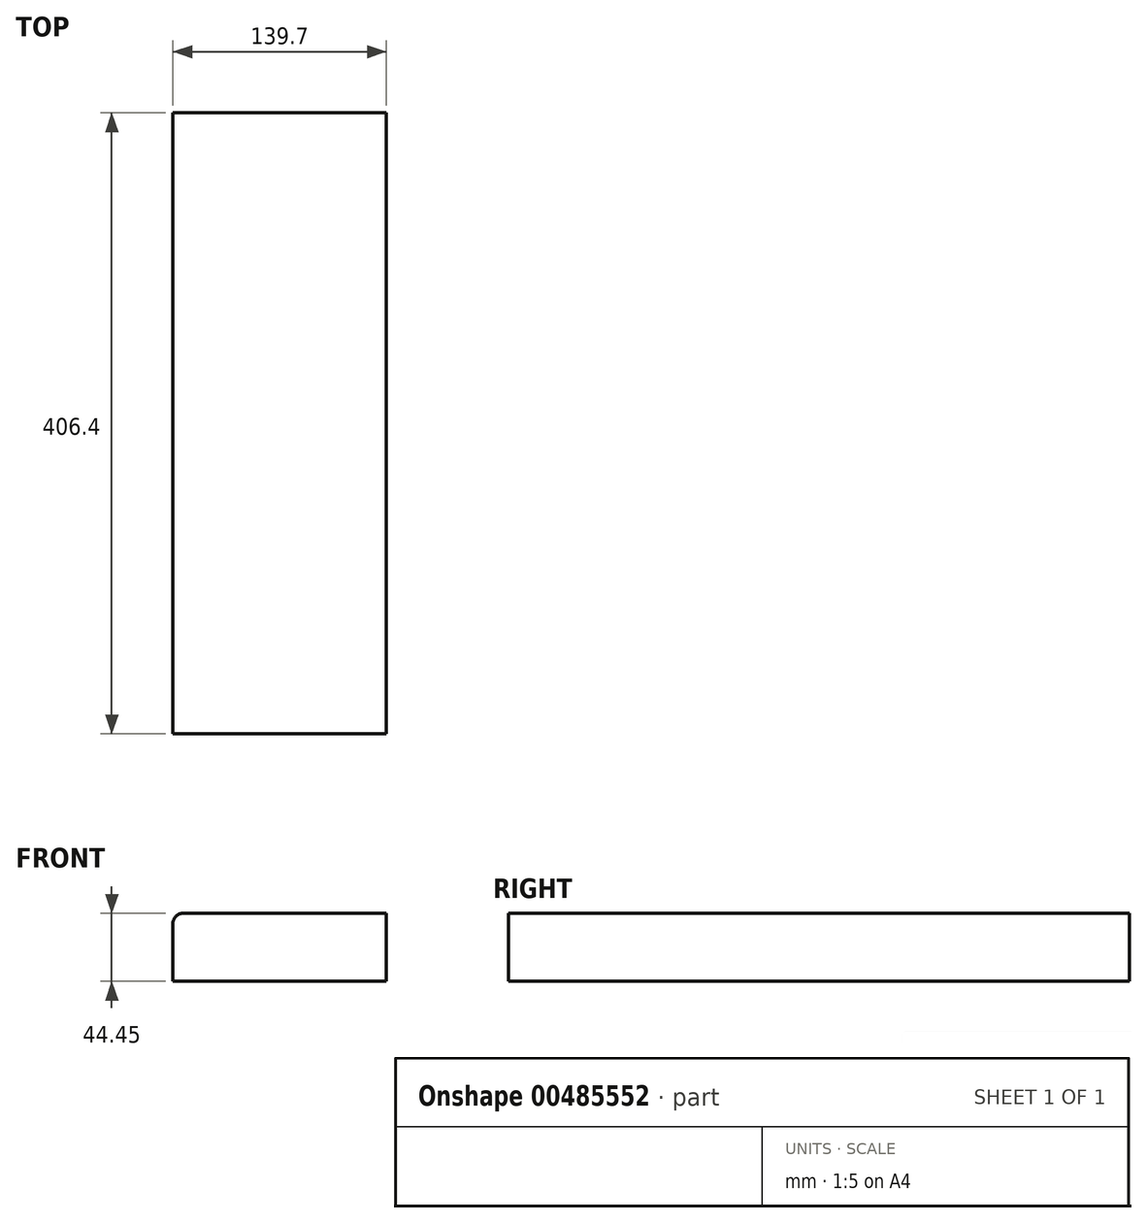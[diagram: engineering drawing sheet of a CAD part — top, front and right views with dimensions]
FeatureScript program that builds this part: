
annotation { "Feature Type Name" : "Feature", "Feature Type Description" : "" }
export const myFeature = defineFeature(function(context is Context, id is Id, definition is map)
    precondition{}
    {
        {
            var Q0;
            Q0=qCreatedBy(makeId("Front.planeOp"),FACE);
            var sketch = newSketch(context, id + "F0", { "sketchPlane" : qUnion([Q0])});
            skLineSegment(sketch, "E0.bottom", {"start": v(0, 0) * mm, "end": v(139.7, 0) * mm});
            skLineSegment(sketch, "E0.top", {"start": v(6.35, 44.45) * mm, "end": v(139.7, 44.45) * mm});
            skLineSegment(sketch, "E0.left", {"start": v(0, 0) * mm, "end": v(0, 38.1) * mm});
            skLineSegment(sketch, "E0.right", {"start": v(139.7, 0) * mm, "end": v(139.7, 44.45) * mm});
            skPoint(sketch, "E1.visualSharp", {"position": v(0, 44.45) * mm});
            skArc(sketch, "E1.filletArc", {"start": v(6.35, 44.45) * mm, "mid": v(1.86, 42.6) * mm, "end": v(0, 38.1) * mm});
            skSolve(sketch);
        }
        {
            var Q0;
            Q0 = qSketchRegion(id + "F0", true);
            extrude(context, id + "F1", {"entities" : qUnion([Q0]), "depth" : 406.4 * mm});
        }
    });
